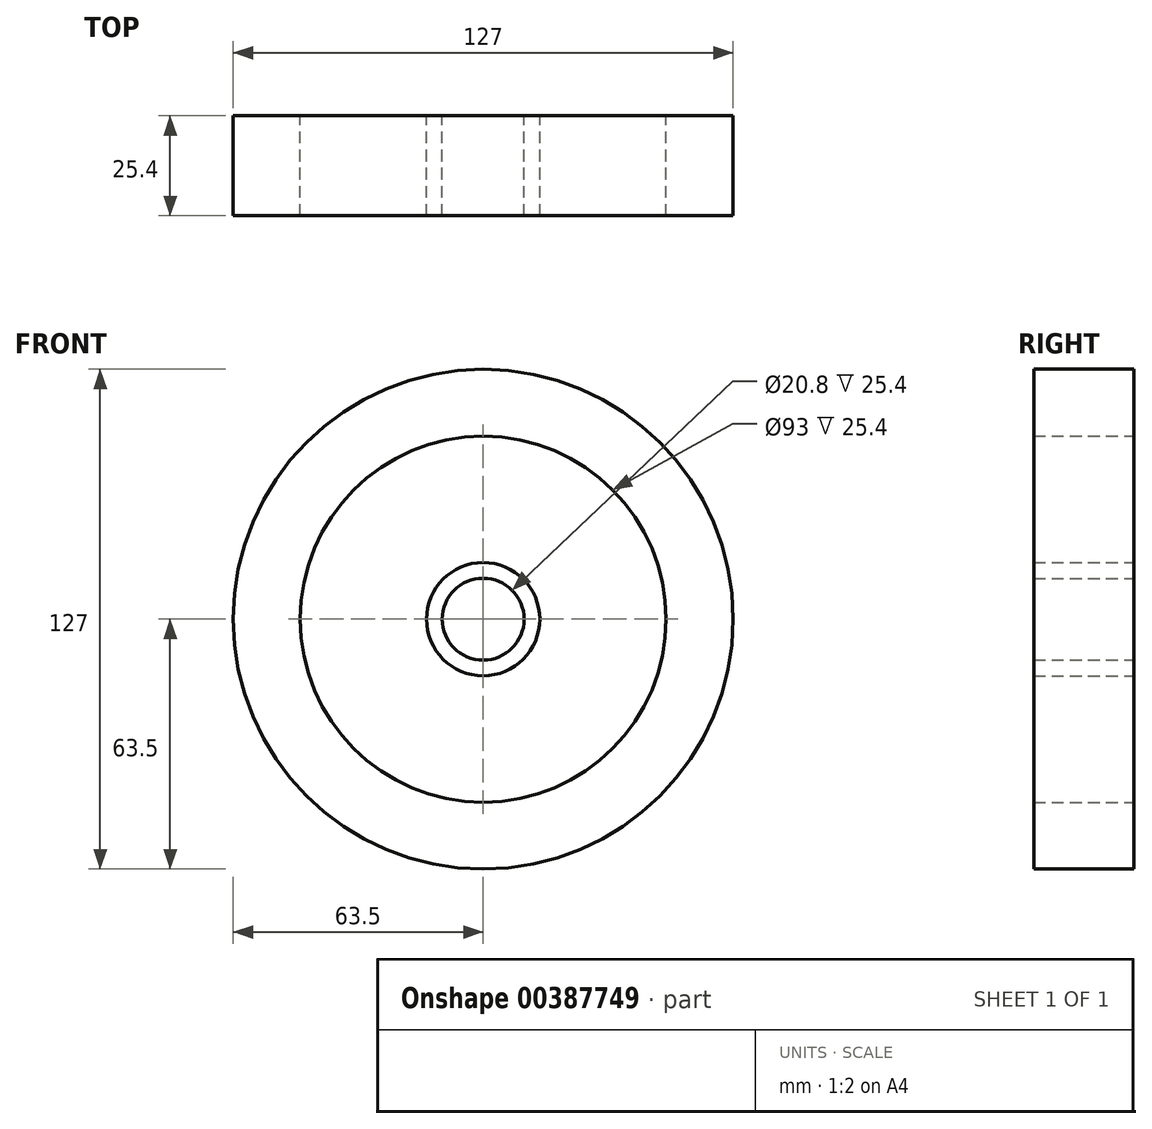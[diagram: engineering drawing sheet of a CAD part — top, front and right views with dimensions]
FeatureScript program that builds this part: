
annotation { "Feature Type Name" : "Feature", "Feature Type Description" : "" }
export const myFeature = defineFeature(function(context is Context, id is Id, definition is map)
    precondition{}
    {
        {
            var Q0;
            Q0=qCreatedBy(makeId("Front.planeOp"),FACE);
            var sketch = newSketch(context, id + "F0", { "sketchPlane" : qUnion([Q0])});
            skCircle(sketch, "E0", {"center": v(0, 0) * mm, "radius": 63.5 * mm});
            skCircle(sketch, "E1", {"center": v(0, 0) * mm, "radius": 46.5 * mm});
            skSolve(sketch);
        }
        {
            var Q0;
            Q0=makeQuery(id+"F0.imprint","IMPRINT",FACE,{"disambiguationData":[TD([[makeQuery(id+"F0.imprint","IMPRINT",EDGE,{"derivedFrom":sQuery(id+"F0.wireOp",EDGE,"E0")}),1.0]])]});
            extrude(context, id + "F1", {"entities" : qUnion([Q0]), "depth" : 25.4 * mm});
        }
        {
            var Q0;
            Q0=qCreatedBy(makeId("Front.planeOp"),FACE);
            var sketch = newSketch(context, id + "F2", { "sketchPlane" : qUnion([Q0])});
            skCircle(sketch, "E2", {"center": v(0, 0) * mm, "radius": 14.39 * mm});
            skCircle(sketch, "E3", {"center": v(0, 0) * mm, "radius": 10.4 * mm});
            skSolve(sketch);
        }
        {
            var Q0;
            Q0=makeQuery(id+"F2.imprint","IMPRINT",FACE,{"disambiguationData":[TD([[makeQuery(id+"F2.imprint","IMPRINT",EDGE,{"derivedFrom":sQuery(id+"F2.wireOp",EDGE,"E2")}),1.0]])]});
            extrude(context, id + "F3", {"entities" : qUnion([Q0]), "depth" : 25.4 * mm});
        }
    });
